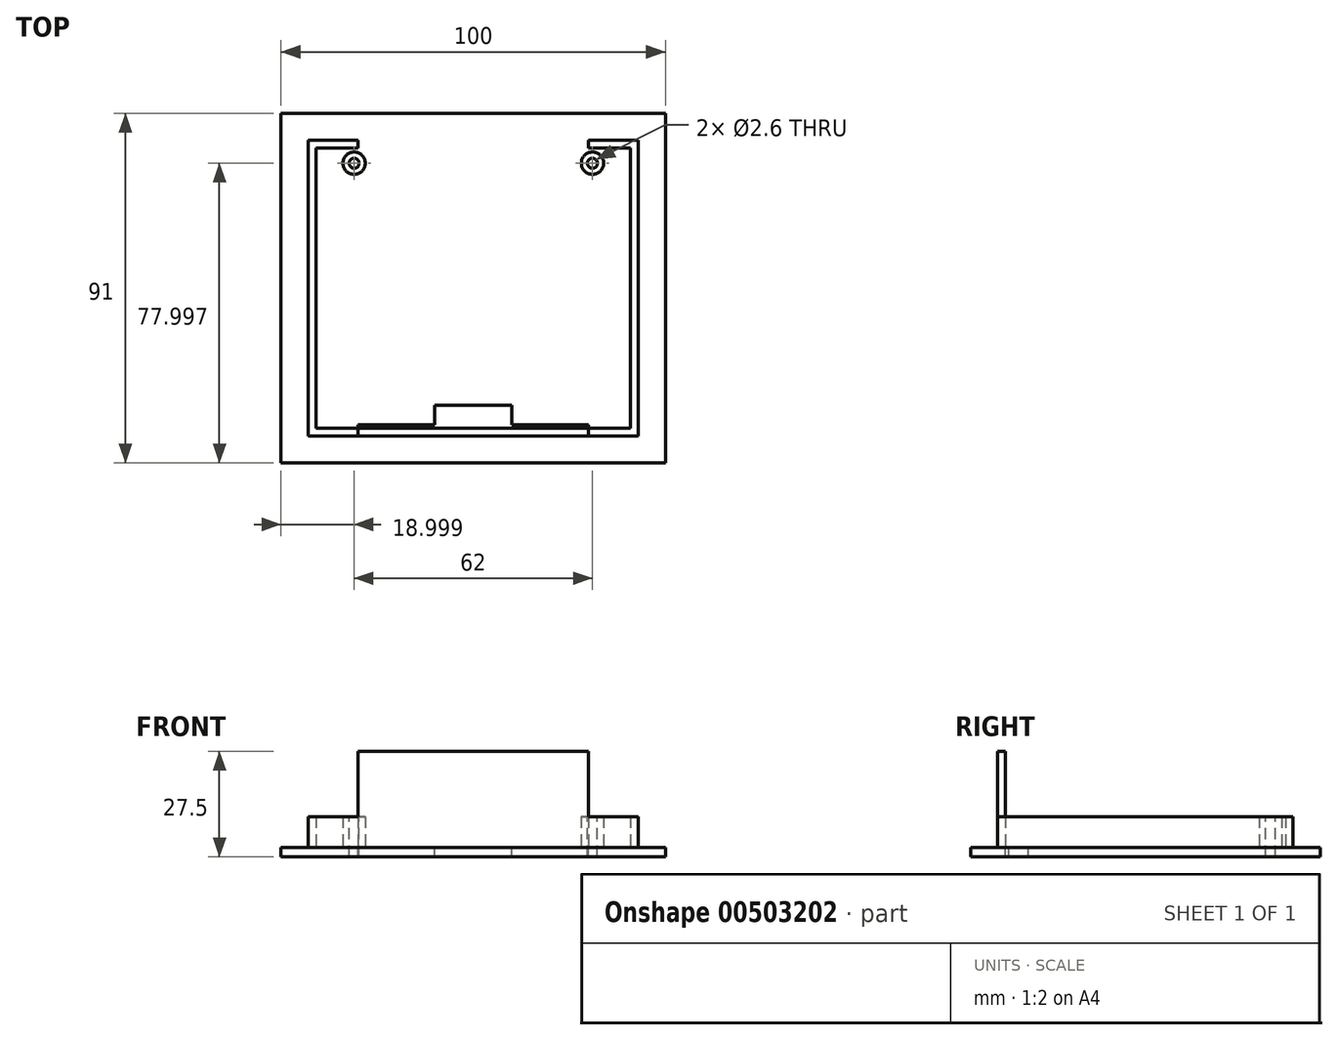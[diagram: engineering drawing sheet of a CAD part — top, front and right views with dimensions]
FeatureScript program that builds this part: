
annotation { "Feature Type Name" : "Feature", "Feature Type Description" : "" }
export const myFeature = defineFeature(function(context is Context, id is Id, definition is map)
    precondition{}
    {
        {
            var Q0;
            Q0=qCreatedBy(makeId("Top.planeOp"),FACE);
            var sketch = newSketch(context, id + "F0", { "sketchPlane" : qUnion([Q0])});
            skLineSegment(sketch, "E0.bottom", {"start": v(1.17, 28.48) * mm, "end": v(81.17, 28.48) * mm});
            skLineSegment(sketch, "E0.top", {"start": v(1.17, -42.52) * mm, "end": v(81.17, -42.52) * mm});
            skLineSegment(sketch, "E0.left", {"start": v(1.17, 28.48) * mm, "end": v(1.17, -42.52) * mm});
            skLineSegment(sketch, "E0.right", {"start": v(81.17, 28.48) * mm, "end": v(81.17, -42.52) * mm});
            skCircle(sketch, "E1", {"center": v(10.17, 25.48) * mm, "radius": 1.3 * mm});
            skCircle(sketch, "E2", {"center": v(72.17, 25.48) * mm, "radius": 1.3 * mm});
            skCircle(sketch, "E3.0", {"center": v(10.17, 25.48) * mm, "radius": 2.9 * mm});
            skCircle(sketch, "E4.0", {"center": v(72.17, 25.48) * mm, "radius": 2.9 * mm});
            skLineSegment(sketch, "E5.bottom", {"start": v(31.17, -42.52) * mm, "end": v(51.17, -42.52) * mm});
            skLineSegment(sketch, "E5.top", {"start": v(31.17, -37.52) * mm, "end": v(51.17, -37.52) * mm});
            skLineSegment(sketch, "E5.left", {"start": v(31.17, -42.52) * mm, "end": v(31.17, -37.52) * mm});
            skLineSegment(sketch, "E5.right", {"start": v(51.17, -42.52) * mm, "end": v(51.17, -37.52) * mm});
            skLineSegment(sketch, "E6.0", {"start": v(-8.83, 38.48) * mm, "end": v(-8.83, -52.52) * mm});
            skLineSegment(sketch, "E6.1", {"start": v(-8.83, 38.48) * mm, "end": v(91.17, 38.48) * mm});
            skLineSegment(sketch, "E6.2", {"start": v(91.17, 38.48) * mm, "end": v(91.17, -52.52) * mm});
            skLineSegment(sketch, "E6.3", {"start": v(-8.83, -52.52) * mm, "end": v(91.17, -52.52) * mm});
            skLineSegment(sketch, "E7.0", {"start": v(0.27, 29.38) * mm, "end": v(0.27, -43.42) * mm});
            skLineSegment(sketch, "E7.1", {"start": v(0.27, 29.38) * mm, "end": v(82.07, 29.38) * mm});
            skLineSegment(sketch, "E7.2", {"start": v(82.07, 29.38) * mm, "end": v(82.07, -43.42) * mm});
            skLineSegment(sketch, "E7.3", {"start": v(0.27, -43.42) * mm, "end": v(82.07, -43.42) * mm});
            skLineSegment(sketch, "E8.0", {"start": v(-1.75, -45.44) * mm, "end": v(84.09, -45.44) * mm});
            skLineSegment(sketch, "E8.1", {"start": v(-1.75, 31.4) * mm, "end": v(-1.75, -45.44) * mm});
            skLineSegment(sketch, "E8.2", {"start": v(-1.75, 31.4) * mm, "end": v(84.09, 31.4) * mm});
            skLineSegment(sketch, "E8.3", {"start": v(84.09, 31.4) * mm, "end": v(84.09, -45.44) * mm});
            skLineSegment(sketch, "E9", {"start": v(11.17, 31.4) * mm, "end": v(11.17, -45.44) * mm});
            skLineSegment(sketch, "E10", {"start": v(71.17, 31.4) * mm, "end": v(71.17, -45.44) * mm});
            skSolve(sketch);
        }
        {
            var Q0;
            Q0=makeQuery(id+"F0.imprint","IMPRINT",FACE,{"disambiguationData":[TD([[makeQuery(id+"F0.imprint","IMPRINT",EDGE,{"derivedFrom":sQuery(id+"F0.wireOp",EDGE,"E0.bottom")}),-1.0]])]});
            var Q1;
            Q1=makeQuery(id+"F0.imprint","IMPRINT",FACE,{"disambiguationData":[TD([[makeQuery(id+"F0.imprint","IMPRINT",EDGE,{"derivedFrom":sQuery(id+"F0.wireOp",EDGE,"E0.bottom")}),1.0]])]});
            var Q2;
            Q2=makeQuery(id+"F0.imprint","IMPRINT",FACE,{"disambiguationData":[TD([[makeQuery(id+"F0.imprint","IMPRINT",EDGE,{"derivedFrom":sQuery(id+"F0.wireOp",EDGE,"E5.bottom")}),1.0]])]});
            var Q3;
            Q3=makeQuery(id+"F0.imprint","IMPRINT",FACE,{"disambiguationData":[TD([[makeQuery(id+"F0.imprint","IMPRINT",EDGE,{"derivedFrom":sQuery(id+"F0.wireOp",EDGE,"E1")}),-1.0]])]});
            var Q4;
            Q4=makeQuery(id+"F0.imprint","IMPRINT",FACE,{"disambiguationData":[TD([[makeQuery(id+"F0.imprint","IMPRINT",EDGE,{"derivedFrom":sQuery(id+"F0.wireOp",EDGE,"E2")}),-1.0]])]});
            var Q5;
            Q5=makeQuery(id+"F0.imprint","IMPRINT",FACE,{"disambiguationData":[TD([[makeQuery(id+"F0.imprint","IMPRINT",EDGE,{"derivedFrom":sQuery(id+"F0.wireOp",EDGE,"E6.0")}),1.0]])]});
            var Q6;
            Q6=makeQuery(id+"F0.imprint","IMPRINT",FACE,{"disambiguationData":[TD([[makeQuery(id+"F0.imprint","IMPRINT",EDGE,{"derivedFrom":sQuery(id+"F0.wireOp",EDGE,"E7.0")}),-1.0]])]});
            var Q7;
            {var subQ0=sQuery(id+"F0.wireOp",EDGE,"E0.left");Q7=makeQuery(id+"F0.imprint","IMPRINT",FACE,{"disambiguationData":[TD([[makeQuery(id+"F0.imprint","IMPRINT",EDGE,{"derivedFrom":subQ0}),-1.0]])]});}
            var Q8;
            Q8=makeQuery(id+"F0.imprint","IMPRINT",FACE,{"disambiguationData":[TD([[makeQuery(id+"F0.imprint","IMPRINT",EDGE,{"derivedFrom":sQuery(id+"F0.wireOp",EDGE,"E5.top")}),1.0]])]});
            var Q9;
            {var subQ5=sQuery(id+"F0.wireOp",EDGE,"E7.2");Q9=makeQuery(id+"F0.imprint","IMPRINT",FACE,{"disambiguationData":[TD([[makeQuery(id+"F0.imprint","IMPRINT",EDGE,{"derivedFrom":subQ5}),1.0]])]});}
            var Q10;
            {var subQ0=sQuery(id+"F0.wireOp",EDGE,"E9");var subQ1=sQuery(id+"F0.wireOp",EDGE,"E7.1");var subQ2=makeQuery(id+"F0.imprint","INTERSECT",VERTEX,{"derivedFrom":[subQ1,subQ0]});Q10=makeQuery(id+"F0.imprint","IMPRINT",FACE,{"disambiguationData":[TD([[makeQuery(id+"F0.imprint","IMPRINT",EDGE,{"disambiguationData":[TD([[subQ2,-1.0]])],"derivedFrom":subQ1}),1.0]])]});}
            var Q11;
            {var subQ0=sQuery(id+"F0.wireOp",EDGE,"E9");var subQ1=sQuery(id+"F0.wireOp",EDGE,"E7.3");var subQ2=makeQuery(id+"F0.imprint","INTERSECT",VERTEX,{"derivedFrom":[subQ1,subQ0]});Q11=makeQuery(id+"F0.imprint","IMPRINT",FACE,{"disambiguationData":[TD([[makeQuery(id+"F0.imprint","IMPRINT",EDGE,{"disambiguationData":[TD([[subQ2,-1.0]])],"derivedFrom":subQ1}),-1.0]])]});}
            var Q12;
            {var subQ5=sQuery(id+"F0.wireOp",EDGE,"E5.bottom");Q12=makeQuery(id+"F0.imprint","IMPRINT",FACE,{"disambiguationData":[TD([[makeQuery(id+"F0.imprint","IMPRINT",EDGE,{"derivedFrom":subQ5}),-1.0]])]});}
            var Q13;
            {var subQ4=sQuery(id+"F0.wireOp",EDGE,"E0.right");Q13=makeQuery(id+"F0.imprint","IMPRINT",FACE,{"disambiguationData":[TD([[makeQuery(id+"F0.imprint","IMPRINT",EDGE,{"derivedFrom":subQ4}),1.0]])]});}
            extrude(context, id + "F1", {"entities" : qUnion([Q0, Q1, Q2, Q3, Q4, Q5, Q6, Q7, Q8, Q9, Q10, Q11, Q12, Q13]), "oppositeDirection" : true, "depth" : 2.5 * mm});
        }
        {
            var Q0;
            Q0=makeQuery(id+"F0.imprint","IMPRINT",FACE,{"disambiguationData":[TD([[makeQuery(id+"F0.imprint","IMPRINT",EDGE,{"derivedFrom":sQuery(id+"F0.wireOp",EDGE,"E5.bottom")}),1.0]])]});
            var Q1;
            Q1=makeQuery(id+"F0.imprint","IMPRINT",FACE,{"disambiguationData":[TD([[makeQuery(id+"F0.imprint","IMPRINT",EDGE,{"derivedFrom":sQuery(id+"F0.wireOp",EDGE,"E1")}),-1.0]])]});
            var Q2;
            Q2=makeQuery(id+"F0.imprint","IMPRINT",FACE,{"disambiguationData":[TD([[makeQuery(id+"F0.imprint","IMPRINT",EDGE,{"derivedFrom":sQuery(id+"F0.wireOp",EDGE,"E2")}),-1.0]])]});
            extrude(context, id + "F2", {"entities" : qUnion([Q0, Q1, Q2]), "operationType" : NewBodyOperationType.ADD, "depth" : 8 * mm});
        }
        {
            var Q0;
            {var subQ5=sQuery(id+"F0.wireOp",EDGE,"E7.0");Q0=makeQuery(id+"F0.imprint","IMPRINT",FACE,{"disambiguationData":[TD([[makeQuery(id+"F0.imprint","IMPRINT",EDGE,{"derivedFrom":subQ5}),-1.0]])]});}
            var Q1;
            {var subQ5=sQuery(id+"F0.wireOp",EDGE,"E7.2");Q1=makeQuery(id+"F0.imprint","IMPRINT",FACE,{"disambiguationData":[TD([[makeQuery(id+"F0.imprint","IMPRINT",EDGE,{"derivedFrom":subQ5}),1.0]])]});}
            extrude(context, id + "F3", {"entities" : qUnion([Q0, Q1]), "operationType" : NewBodyOperationType.ADD, "depth" : 8 * mm});
        }
        {
            var Q0;
            {var subQ0=sQuery(id+"F0.wireOp",EDGE,"E9");var subQ1=sQuery(id+"F0.wireOp",EDGE,"E7.3");var subQ2=makeQuery(id+"F0.imprint","INTERSECT",VERTEX,{"derivedFrom":[subQ1,subQ0]});Q0=makeQuery(id+"F0.imprint","IMPRINT",FACE,{"disambiguationData":[TD([[makeQuery(id+"F0.imprint","IMPRINT",EDGE,{"disambiguationData":[TD([[subQ2,-1.0]])],"derivedFrom":subQ1}),-1.0]])]});}
            extrude(context, id + "F4", {"entities" : qUnion([Q0]), "operationType" : NewBodyOperationType.ADD, "depth" : 25 * mm});
        }
    });
